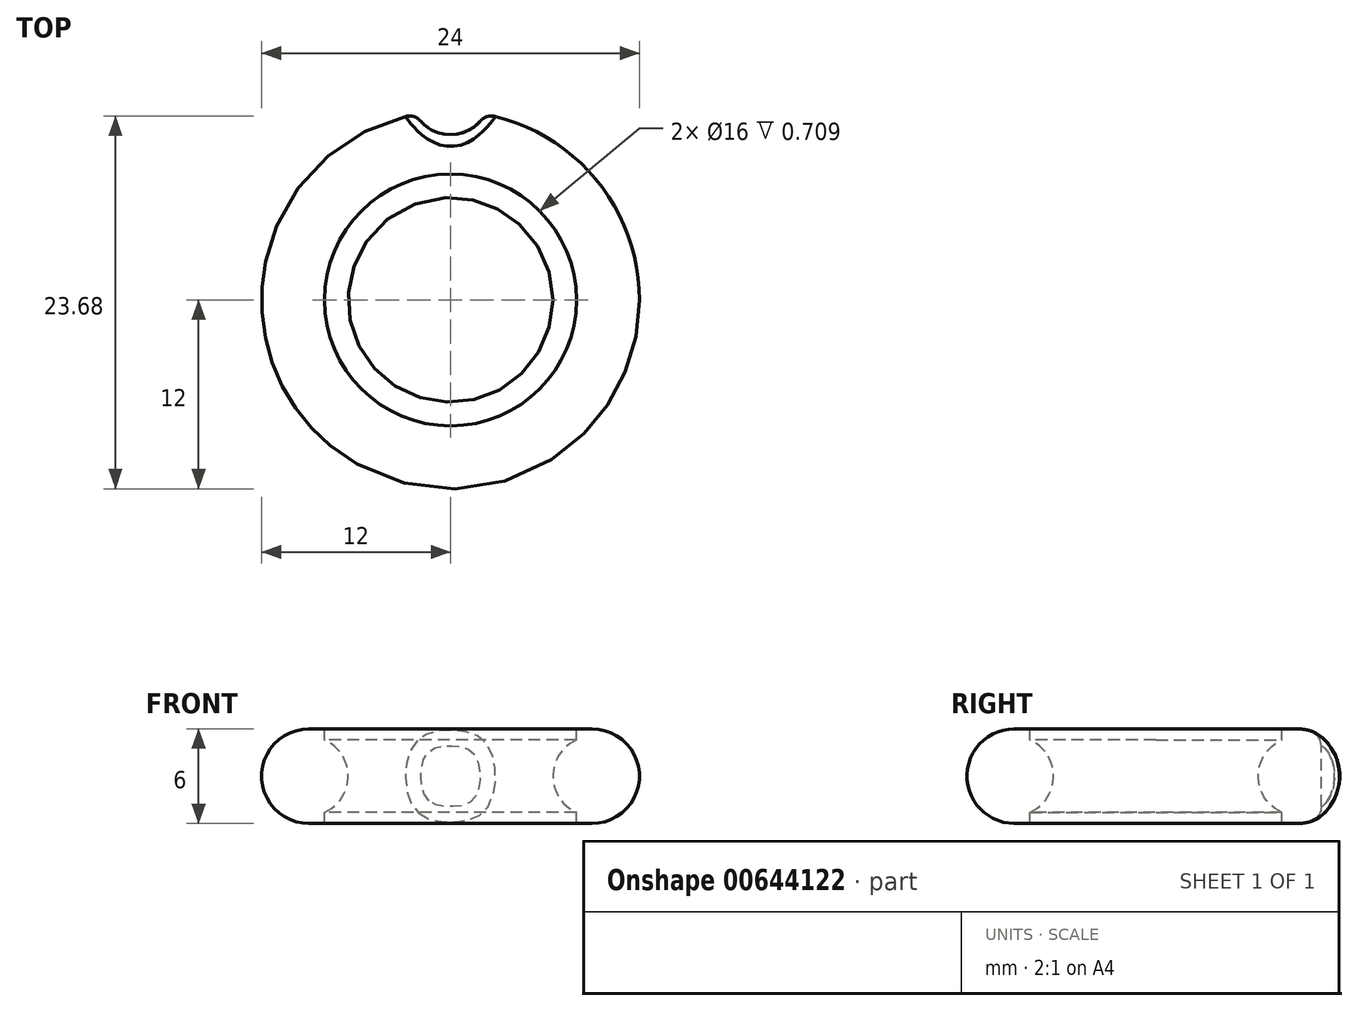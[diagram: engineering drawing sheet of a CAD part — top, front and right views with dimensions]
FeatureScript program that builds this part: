
annotation { "Feature Type Name" : "Feature", "Feature Type Description" : "" }
export const myFeature = defineFeature(function(context is Context, id is Id, definition is map)
    precondition{}
    {
        {
            var Q0;
            Q0=qCreatedBy(makeId("Front.planeOp"),FACE);
            var sketch = newSketch(context, id + "F0", { "sketchPlane" : qUnion([Q0])});
            skArc(sketch, "E0", {"start": v(-9, 3) * mm, "mid": v(-12, 0) * mm, "end": v(-9, -3) * mm});
            skLineSegment(sketch, "E1", {"start": v(0, 3) * mm, "end": v(0, -3) * mm});
            skLineSegment(sketch, "E2", {"start": v(0, -3) * mm, "end": v(-9, -3) * mm});
            skLineSegment(sketch, "E3", {"start": v(0, 3) * mm, "end": v(-9, 3) * mm});
            skSolve(sketch);
        }
        {
            var Q0;
            Q0 = qSketchRegion(id + "F0", true);
            var Q1;
            Q1=sQuery(id+"F0.wireOp",EDGE,"E1");
            revolve(context, id + "F1", {"entities" : qUnion([Q0]), "axis" : qUnion([Q1]), "revolveType" : RevolveType.FULL});
        }
        {
            var Q0;
            Q0=qCreatedBy(makeId("Top.planeOp"),FACE);
            cPlane(context, id + "F2", {"entities" : qUnion([Q0]), "cplaneType" : CPlaneType.OFFSET, "offset" : 5 * mm, "width" : 150 * mm, "height" : 150 * mm});
        }
        {
            var Q0;
            Q0=qCreatedBy(id+"F2.planeOp",FACE);
            var sketch = newSketch(context, id + "F3", { "sketchPlane" : qUnion([Q0])});
            skCircle(sketch, "E4", {"center": v(0, 0) * mm, "radius": 8 * mm});
            skSolve(sketch);
        }
        {
            var Q0;
            Q0 = qSketchRegion(id + "F3", true);
            extrude(context, id + "F4", {"entities" : qUnion([Q0]), "operationType" : NewBodyOperationType.REMOVE, "oppositeDirection" : true, "depth" : 25 * mm, "offsetDistance" : 25 * mm});
        }
        {
            var Q0;
            Q0=qCreatedBy(makeId("Front.planeOp"),FACE);
            var sketch = newSketch(context, id + "F5", { "sketchPlane" : qUnion([Q0])});
            skCircle(sketch, "E5", {"center": v(-9, 0) * mm, "radius": 2.5 * mm});
            skSolve(sketch);
        }
        {
            var Q0;
            Q0 = qSketchRegion(id + "F5", true);
            var Q1;
            Q1=sQuery(id+"F0.wireOp",EDGE,"E1");
            revolve(context, id + "F6", {"operationType" : NewBodyOperationType.ADD, "entities" : qUnion([Q0]), "axis" : qUnion([Q1]), "revolveType" : RevolveType.FULL});
        }
        {
            var Q0;
            Q0=qCreatedBy(id+"F2.planeOp",FACE);
            var sketch = newSketch(context, id + "F7", { "sketchPlane" : qUnion([Q0])});
            skCircle(sketch, "E6", {"center": v(0, 13) * mm, "radius": 2.5 * mm});
            skSolve(sketch);
        }
        {
            var Q0;
            Q0 = qSketchRegion(id + "F7", true);
            extrude(context, id + "F8", {"entities" : qUnion([Q0]), "operationType" : NewBodyOperationType.REMOVE, "oppositeDirection" : true, "depth" : 25 * mm, "offsetDistance" : 25 * mm});
        }
        {
            var Q0;
            Q0=makeQuery(id+"F8.boolean.opBoolean","INTERSECT",EDGE,{"derivedFrom":[makeQuery(id+"F1.opRevolve","SWEPT_FACE",FACE,{"disambiguationData":[OSD([sQuery(id+"F0.wireOp",EDGE,"E0")])]}),makeQuery(id+"F8.opExtrude","SWEPT_FACE",FACE,{"disambiguationData":[OSD([sQuery(id+"F7.wireOp",EDGE,"E6")])]})]});
            fillet(context, id + "F9", {"entities" : qUnion([Q0]), "radius" : 1 * mm, "tangentPropagation" : true, "allowEdgeOverflow" : false});
        }
    });
